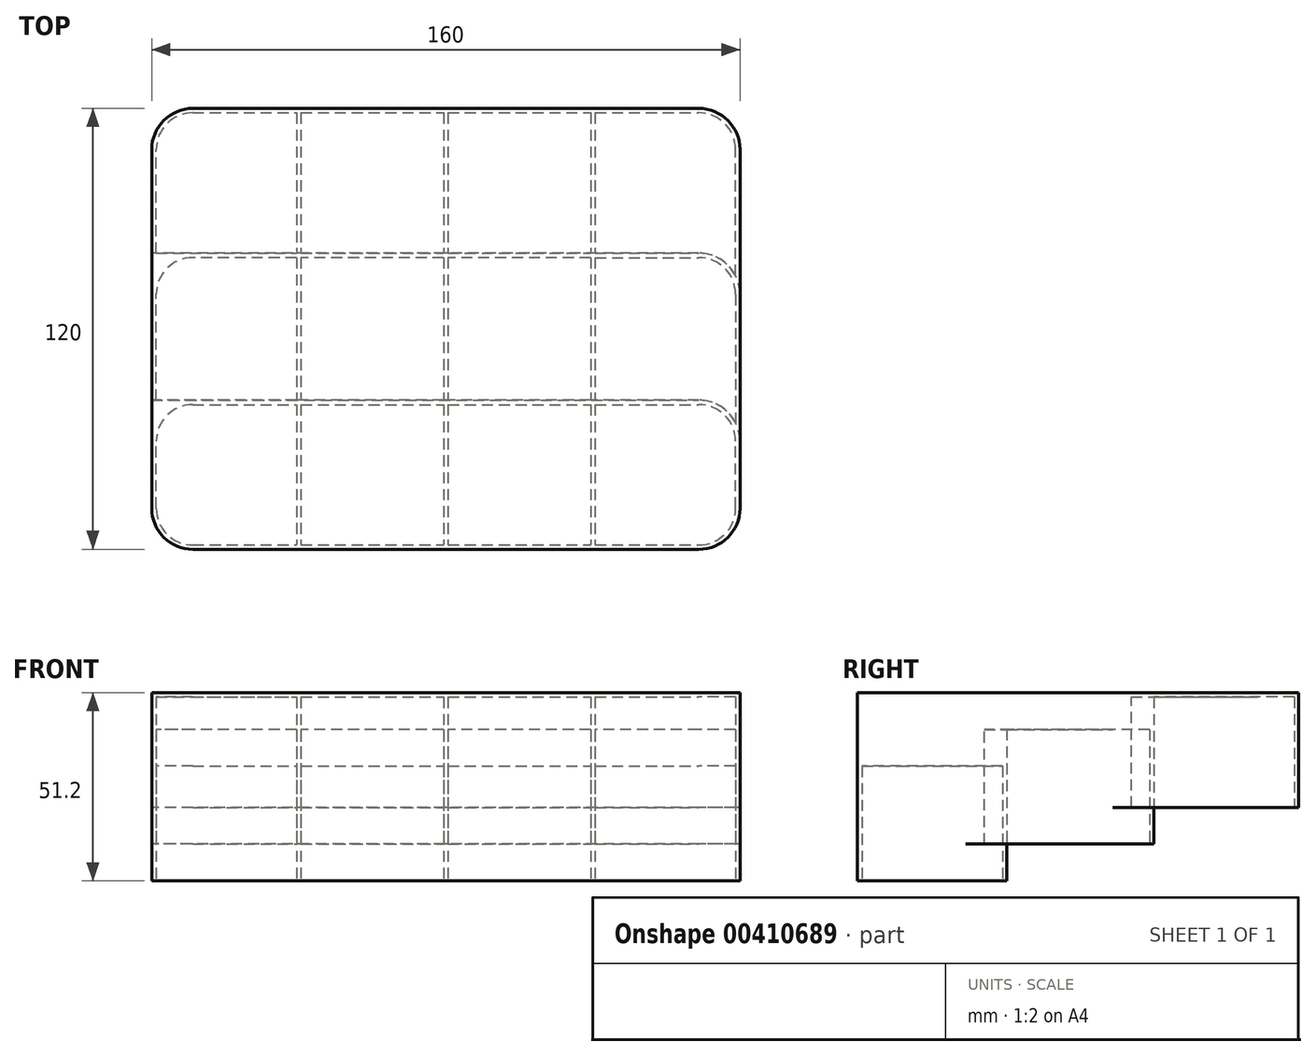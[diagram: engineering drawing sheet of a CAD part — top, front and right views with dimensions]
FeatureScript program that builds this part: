
annotation { "Feature Type Name" : "Feature", "Feature Type Description" : "" }
export const myFeature = defineFeature(function(context is Context, id is Id, definition is map)
    precondition{}
    {
        {
            var Q0;
            Q0=qCreatedBy(makeId("Top.planeOp"),FACE);
            var sketch = newSketch(context, id + "F0", { "sketchPlane" : qUnion([Q0])});
            skLineSegment(sketch, "E0.bottom", {"start": v(-160, -120) * mm, "end": v(0, -120) * mm});
            skLineSegment(sketch, "E0.top", {"start": v(-160, 0) * mm, "end": v(0, 0) * mm});
            skLineSegment(sketch, "E0.left", {"start": v(-160, -120) * mm, "end": v(-160, 0) * mm});
            skLineSegment(sketch, "E0.right", {"start": v(0, -120) * mm, "end": v(0, 0) * mm});
            skLineSegment(sketch, "E1.0", {"start": v(-158.8, -1.2) * mm, "end": v(-120.6, -1.2) * mm});
            skLineSegment(sketch, "E2.0", {"start": v(-158.8, -118.8) * mm, "end": v(-158.8, -80.6) * mm});
            skLineSegment(sketch, "E3.0", {"start": v(-158.8, -118.8) * mm, "end": v(-120.6, -118.8) * mm});
            skLineSegment(sketch, "E4.0", {"start": v(-1.2, -118.8) * mm, "end": v(-1.2, -80.6) * mm});
            skLineSegment(sketch, "E5.0", {"start": v(-158.8, -40.6) * mm, "end": v(-120.6, -40.6) * mm});
            skLineSegment(sketch, "E6.0", {"start": v(-158.8, -80.6) * mm, "end": v(-120.6, -80.6) * mm});
            skLineSegment(sketch, "E7.0", {"start": v(-158.8, -79.4) * mm, "end": v(-120.6, -79.4) * mm});
            skLineSegment(sketch, "E8.0", {"start": v(-158.8, -39.4) * mm, "end": v(-120.6, -39.4) * mm});
            skLineSegment(sketch, "E9.0", {"start": v(-120.6, -1.2) * mm, "end": v(-120.6, -39.4) * mm});
            skLineSegment(sketch, "E10.0", {"start": v(-119.4, -1.2) * mm, "end": v(-119.4, -39.4) * mm});
            skLineSegment(sketch, "E11.0", {"start": v(-80.6, -1.2) * mm, "end": v(-80.6, -39.4) * mm});
            skLineSegment(sketch, "E12.0", {"start": v(-79.4, -1.2) * mm, "end": v(-79.4, -39.4) * mm});
            skLineSegment(sketch, "E13.0", {"start": v(-40.6, -1.2) * mm, "end": v(-40.6, -39.4) * mm});
            skLineSegment(sketch, "E14.0", {"start": v(-39.4, -1.2) * mm, "end": v(-39.4, -39.4) * mm});
            skPoint(sketch, "E15.orphan", {"position": v(-160, -40) * mm});
            skLineSegment(sketch, "E16.trimOffspring", {"start": v(-158.8, -79.4) * mm, "end": v(-158.8, -40.6) * mm});
            skPoint(sketch, "E17.orphan", {"position": v(-160, -80) * mm});
            skPoint(sketch, "E18.orphan", {"position": v(-120, -120) * mm});
            skPoint(sketch, "E19.orphan", {"position": v(-80, -120) * mm});
            skPoint(sketch, "E20.orphan", {"position": v(0, -40) * mm});
            skLineSegment(sketch, "E21.trimOffspring", {"start": v(-119.4, -39.4) * mm, "end": v(-80.6, -39.4) * mm});
            skLineSegment(sketch, "E22.trimOffspring", {"start": v(-119.4, -40.6) * mm, "end": v(-80.6, -40.6) * mm});
            skLineSegment(sketch, "E23.trimOffspring", {"start": v(-120.6, -40.6) * mm, "end": v(-120.6, -79.4) * mm});
            skLineSegment(sketch, "E24.trimOffspring", {"start": v(-119.4, -40.6) * mm, "end": v(-119.4, -79.4) * mm});
            skLineSegment(sketch, "E25.trimOffspring", {"start": v(-119.4, -79.4) * mm, "end": v(-80.6, -79.4) * mm});
            skLineSegment(sketch, "E26.trimOffspring", {"start": v(-120.6, -80.6) * mm, "end": v(-120.6, -118.8) * mm});
            skLineSegment(sketch, "E27.trimOffspring", {"start": v(-119.4, -80.6) * mm, "end": v(-119.4, -118.8) * mm});
            skLineSegment(sketch, "E28.trimOffspring", {"start": v(-119.4, -80.6) * mm, "end": v(-80.6, -80.6) * mm});
            skLineSegment(sketch, "E29.trimOffspring", {"start": v(-80.6, -40.6) * mm, "end": v(-80.6, -79.4) * mm});
            skLineSegment(sketch, "E30.trimOffspring", {"start": v(-79.4, -39.4) * mm, "end": v(-40.6, -39.4) * mm});
            skLineSegment(sketch, "E31.trimOffspring", {"start": v(-79.4, -40.6) * mm, "end": v(-79.4, -79.4) * mm});
            skLineSegment(sketch, "E32.trimOffspring", {"start": v(-79.4, -40.6) * mm, "end": v(-40.6, -40.6) * mm});
            skLineSegment(sketch, "E33.trimOffspring", {"start": v(-40.6, -40.6) * mm, "end": v(-40.6, -79.4) * mm});
            skLineSegment(sketch, "E34.trimOffspring", {"start": v(-39.4, -39.4) * mm, "end": v(-1.2, -39.4) * mm});
            skLineSegment(sketch, "E35.trimOffspring", {"start": v(-39.4, -40.6) * mm, "end": v(-1.2, -40.6) * mm});
            skLineSegment(sketch, "E36.trimOffspring", {"start": v(-39.4, -40.6) * mm, "end": v(-39.4, -79.4) * mm});
            skLineSegment(sketch, "E37.trimOffspring", {"start": v(-39.4, -79.4) * mm, "end": v(-1.2, -79.4) * mm});
            skLineSegment(sketch, "E38.trimOffspring", {"start": v(-39.4, -80.6) * mm, "end": v(-1.2, -80.6) * mm});
            skLineSegment(sketch, "E39.trimOffspring", {"start": v(-39.4, -80.6) * mm, "end": v(-39.4, -118.8) * mm});
            skLineSegment(sketch, "E40.trimOffspring", {"start": v(-40.6, -80.6) * mm, "end": v(-40.6, -118.8) * mm});
            skLineSegment(sketch, "E41.trimOffspring", {"start": v(-79.4, -79.4) * mm, "end": v(-40.6, -79.4) * mm});
            skLineSegment(sketch, "E42.trimOffspring", {"start": v(-79.4, -80.6) * mm, "end": v(-40.6, -80.6) * mm});
            skLineSegment(sketch, "E43.trimOffspring", {"start": v(-80.6, -80.6) * mm, "end": v(-80.6, -118.8) * mm});
            skLineSegment(sketch, "E44.trimOffspring", {"start": v(-79.4, -80.6) * mm, "end": v(-79.4, -118.8) * mm});
            skLineSegment(sketch, "E45.trimOffspring", {"start": v(-1.2, -79.4) * mm, "end": v(-1.2, -40.6) * mm});
            skLineSegment(sketch, "E46.trimOffspring", {"start": v(-1.2, -39.4) * mm, "end": v(-1.2, -1.2) * mm});
            skLineSegment(sketch, "E47.trimOffspring", {"start": v(-39.4, -1.2) * mm, "end": v(-1.2, -1.2) * mm});
            skLineSegment(sketch, "E48.trimOffspring", {"start": v(-79.4, -1.2) * mm, "end": v(-40.6, -1.2) * mm});
            skLineSegment(sketch, "E49.trimOffspring", {"start": v(-119.4, -1.2) * mm, "end": v(-80.6, -1.2) * mm});
            skLineSegment(sketch, "E50.trimOffspring", {"start": v(-158.8, -39.4) * mm, "end": v(-158.8, -1.2) * mm});
            skLineSegment(sketch, "E51.trimOffspring", {"start": v(-119.4, -118.8) * mm, "end": v(-80.6, -118.8) * mm});
            skLineSegment(sketch, "E52.trimOffspring", {"start": v(-79.4, -118.8) * mm, "end": v(-40.6, -118.8) * mm});
            skLineSegment(sketch, "E53.trimOffspring", {"start": v(-39.4, -118.8) * mm, "end": v(-1.2, -118.8) * mm});
            skSolve(sketch);
        }
        {
            var Q0;
            Q0=makeQuery(id+"F0.imprint","IMPRINT",FACE,{"disambiguationData":[TD([[makeQuery(id+"F0.imprint","IMPRINT",EDGE,{"derivedFrom":sQuery(id+"F0.wireOp",EDGE,"E0.bottom")}),1.0]])]});
            extrude(context, id + "F1", {"entities" : qUnion([Q0]), "depth" : 50 * mm});
        }
        {
            var Q0;
            Q0=makeQuery(id+"F1.opExtrude","CAP_FACE",FACE,{"disambiguationData":[OSD([sQuery(id+"F0.wireOp",EDGE,"E0.bottom"),sQuery(id+"F0.wireOp",EDGE,"E0.top"),sQuery(id+"F0.wireOp",EDGE,"E0.left"),sQuery(id+"F0.wireOp",EDGE,"E0.right"),sQuery(id+"F0.wireOp",EDGE,"E1.0"),sQuery(id+"F0.wireOp",EDGE,"E2.0"),sQuery(id+"F0.wireOp",EDGE,"E3.0"),sQuery(id+"F0.wireOp",EDGE,"E4.0"),sQuery(id+"F0.wireOp",EDGE,"E5.0"),sQuery(id+"F0.wireOp",EDGE,"E6.0"),sQuery(id+"F0.wireOp",EDGE,"E7.0"),sQuery(id+"F0.wireOp",EDGE,"E8.0"),sQuery(id+"F0.wireOp",EDGE,"E9.0"),sQuery(id+"F0.wireOp",EDGE,"E10.0"),sQuery(id+"F0.wireOp",EDGE,"E11.0"),sQuery(id+"F0.wireOp",EDGE,"E12.0"),sQuery(id+"F0.wireOp",EDGE,"E13.0"),sQuery(id+"F0.wireOp",EDGE,"E14.0"),sQuery(id+"F0.wireOp",EDGE,"E16.trimOffspring"),sQuery(id+"F0.wireOp",EDGE,"E21.trimOffspring"),sQuery(id+"F0.wireOp",EDGE,"E22.trimOffspring"),sQuery(id+"F0.wireOp",EDGE,"E23.trimOffspring"),sQuery(id+"F0.wireOp",EDGE,"E24.trimOffspring"),sQuery(id+"F0.wireOp",EDGE,"E25.trimOffspring"),sQuery(id+"F0.wireOp",EDGE,"E26.trimOffspring"),sQuery(id+"F0.wireOp",EDGE,"E27.trimOffspring"),sQuery(id+"F0.wireOp",EDGE,"E28.trimOffspring"),sQuery(id+"F0.wireOp",EDGE,"E29.trimOffspring"),sQuery(id+"F0.wireOp",EDGE,"E30.trimOffspring"),sQuery(id+"F0.wireOp",EDGE,"E31.trimOffspring"),sQuery(id+"F0.wireOp",EDGE,"E32.trimOffspring"),sQuery(id+"F0.wireOp",EDGE,"E33.trimOffspring"),sQuery(id+"F0.wireOp",EDGE,"E34.trimOffspring"),sQuery(id+"F0.wireOp",EDGE,"E35.trimOffspring"),sQuery(id+"F0.wireOp",EDGE,"E36.trimOffspring"),sQuery(id+"F0.wireOp",EDGE,"E37.trimOffspring"),sQuery(id+"F0.wireOp",EDGE,"E38.trimOffspring"),sQuery(id+"F0.wireOp",EDGE,"E39.trimOffspring"),sQuery(id+"F0.wireOp",EDGE,"E40.trimOffspring"),sQuery(id+"F0.wireOp",EDGE,"E41.trimOffspring"),sQuery(id+"F0.wireOp",EDGE,"E42.trimOffspring"),sQuery(id+"F0.wireOp",EDGE,"E43.trimOffspring"),sQuery(id+"F0.wireOp",EDGE,"E44.trimOffspring"),sQuery(id+"F0.wireOp",EDGE,"E45.trimOffspring"),sQuery(id+"F0.wireOp",EDGE,"E46.trimOffspring"),sQuery(id+"F0.wireOp",EDGE,"E47.trimOffspring"),sQuery(id+"F0.wireOp",EDGE,"E48.trimOffspring"),sQuery(id+"F0.wireOp",EDGE,"E49.trimOffspring"),sQuery(id+"F0.wireOp",EDGE,"E50.trimOffspring"),sQuery(id+"F0.wireOp",EDGE,"E51.trimOffspring"),sQuery(id+"F0.wireOp",EDGE,"E52.trimOffspring"),sQuery(id+"F0.wireOp",EDGE,"E53.trimOffspring")])],"isStart":false});
            var sketch = newSketch(context, id + "F2", { "sketchPlane" : qUnion([Q0])});
            skLineSegment(sketch, "E54.bottom", {"start": v(-160, 0) * mm, "end": v(0, 0) * mm});
            skLineSegment(sketch, "E54.top", {"start": v(-160, -120) * mm, "end": v(0, -120) * mm});
            skLineSegment(sketch, "E54.left", {"start": v(-160, 0) * mm, "end": v(-160, -120) * mm});
            skLineSegment(sketch, "E54.right", {"start": v(0, 0) * mm, "end": v(0, -120) * mm});
            skSolve(sketch);
        }
        {
            var Q0;
            Q0 = qSketchRegion(id + "F2", true);
            extrude(context, id + "F3", {"entities" : qUnion([Q0]), "operationType" : NewBodyOperationType.ADD, "depth" : 1.2 * mm});
        }
        {
            var Q0;
            Q0=makeQuery(id+"F3.boolean.opBoolean","MERGE",FACE,{"derivedFrom":[makeQuery(id+"F1.opExtrude","SWEPT_FACE",FACE,{"disambiguationData":[OSD([sQuery(id+"F0.wireOp",EDGE,"E0.left")])]}),makeQuery(id+"F3.opExtrude","SWEPT_FACE",FACE,{"disambiguationData":[OSD([sQuery(id+"F2.wireOp",EDGE,"E54.left")])]})]});
            var sketch = newSketch(context, id + "F4", { "sketchPlane" : qUnion([Q0])});
            skLineSegment(sketch, "E55.0.0", {"start": v(79.4, 0) * mm, "end": v(40.6, 0) * mm, "construction": true});
            skLineSegment(sketch, "E55.0.1", {"start": v(40.6, 10) * mm, "end": v(40.6, 50) * mm, "construction": true});
            skLineSegment(sketch, "E55.0.2", {"start": v(40.6, 50) * mm, "end": v(79.4, 50) * mm, "construction": true});
            skLineSegment(sketch, "E55.0.3", {"start": v(79.4, 50) * mm, "end": v(79.4, 0) * mm, "construction": true});
            skLineSegment(sketch, "E56.0.0", {"start": v(39.4, 0) * mm, "end": v(1.2, 0) * mm, "construction": true});
            skLineSegment(sketch, "E56.0.1", {"start": v(1.2, 20) * mm, "end": v(1.2, 50) * mm, "construction": true});
            skLineSegment(sketch, "E56.0.2", {"start": v(1.2, 50) * mm, "end": v(39.4, 50) * mm, "construction": true});
            skLineSegment(sketch, "E56.0.3", {"start": v(39.4, 50) * mm, "end": v(39.4, 10) * mm, "construction": true});
            skLineSegment(sketch, "E57", {"start": v(79.4, 0) * mm, "end": v(79.4, 10) * mm, "construction": true});
            skLineSegment(sketch, "E58", {"start": v(79.4, 10) * mm, "end": v(39.4, 10) * mm, "construction": true});
            skLineSegment(sketch, "E59", {"start": v(39.4, 10) * mm, "end": v(39.4, 20) * mm, "construction": true});
            skLineSegment(sketch, "E60", {"start": v(39.4, 20) * mm, "end": v(0, 20) * mm, "construction": true});
            skLineSegment(sketch, "E61", {"start": v(79.4, 10) * mm, "end": v(39.4, 10) * mm});
            skLineSegment(sketch, "E62", {"start": v(39.4, 20) * mm, "end": v(39.4, 10) * mm});
            skLineSegment(sketch, "E63", {"start": v(39.4, 20) * mm, "end": v(0, 20) * mm});
            skLineSegment(sketch, "E64", {"start": v(0, 20) * mm, "end": v(0, 0) * mm});
            skLineSegment(sketch, "E65", {"start": v(0, 0) * mm, "end": v(79.4, 0) * mm});
            skLineSegment(sketch, "E66", {"start": v(79.4, 10) * mm, "end": v(79.4, 0) * mm});
            skSolve(sketch);
        }
        {
            var Q0;
            Q0=makeQuery(id+"F4.imprint","IMPRINT",FACE,{"disambiguationData":[TD([[makeQuery(id+"F4.imprint","IMPRINT",EDGE,{"derivedFrom":sQuery(id+"F4.wireOp",EDGE,"E61")}),1.0]])]});
            extrude(context, id + "F5", {"entities" : qUnion([Q0]), "operationType" : NewBodyOperationType.REMOVE, "endBound" : BoundingType.THROUGH_ALL, "oppositeDirection" : true, "depth" : 25 * mm});
        }
        {
            var Q0;
            Q0=makeQuery(id+"F3.boolean.opBoolean","MERGE",FACE,{"derivedFrom":[makeQuery(id+"F1.opExtrude","SWEPT_FACE",FACE,{"disambiguationData":[OSD([sQuery(id+"F0.wireOp",EDGE,"E0.left")])]}),makeQuery(id+"F3.opExtrude","SWEPT_FACE",FACE,{"disambiguationData":[OSD([sQuery(id+"F2.wireOp",EDGE,"E54.left")])]})]});
            var sketch = newSketch(context, id + "F6", { "sketchPlane" : qUnion([Q0])});
            skLineSegment(sketch, "E67.0.0", {"start": v(80.6, 0) * mm, "end": v(118.8, 0) * mm});
            skLineSegment(sketch, "E67.0.1", {"start": v(118.8, 31.2) * mm, "end": v(118.8, 50) * mm});
            skLineSegment(sketch, "E67.0.2", {"start": v(118.8, 50) * mm, "end": v(40.6, 50) * mm});
            skLineSegment(sketch, "E68.0.0", {"start": v(40.6, 50) * mm, "end": v(40.6, 10) * mm});
            skLineSegment(sketch, "E68.0.1", {"start": v(40.6, 10) * mm, "end": v(79.4, 10) * mm});
            skLineSegment(sketch, "E68.0.2", {"start": v(79.4, 31.2) * mm, "end": v(79.4, 41.2) * mm});
            skLineSegment(sketch, "E69", {"start": v(118.8, 31.2) * mm, "end": v(79.4, 31.2) * mm});
            skLineSegment(sketch, "E70", {"start": v(79.4, 41.2) * mm, "end": v(40.6, 41.2) * mm});
            skPoint(sketch, "E71.orphan", {"position": v(80.6, 50) * mm});
            skSolve(sketch);
        }
        {
            var Q0;
            Q0=makeQuery(id+"F6.imprint","IMPRINT",FACE,{"disambiguationData":[TD([[makeQuery(id+"F6.imprint","IMPRINT",EDGE,{"derivedFrom":sQuery(id+"F6.wireOp",EDGE,"E67.0.1")}),1.0]])]});
            var Q1;
            Q1=makeQuery(id+"F1.opExtrude","SWEPT_FACE",FACE,{"disambiguationData":[OSD([sQuery(id+"F0.wireOp",EDGE,"E45.trimOffspring")])]});
            extrude(context, id + "F7", {"entities" : qUnion([Q0]), "operationType" : NewBodyOperationType.ADD, "endBound" : BoundingType.UP_TO_SURFACE, "oppositeDirection" : true, "endBoundEntityFace" : qUnion([Q1]), "depth" : 25 * mm});
        }
        {
            var Q0;
            Q0=makeQuery(id+"F1.opExtrude","SWEPT_EDGE",EDGE,{"disambiguationData":[OSD([sQuery(id+"F0.wireOp",EDGE,"E4.0"),sQuery(id+"F0.wireOp",EDGE,"E53.trimOffspring")])]});
            var Q1;
            Q1=makeQuery(id+"F1.opExtrude","SWEPT_EDGE",EDGE,{"disambiguationData":[OSD([sQuery(id+"F0.wireOp",EDGE,"E46.trimOffspring"),sQuery(id+"F0.wireOp",EDGE,"E47.trimOffspring")])]});
            var Q2;
            Q2=makeQuery(id+"F1.opExtrude","SWEPT_EDGE",EDGE,{"disambiguationData":[OSD([sQuery(id+"F0.wireOp",EDGE,"E2.0"),sQuery(id+"F0.wireOp",EDGE,"E3.0")])]});
            var Q3;
            Q3=makeQuery(id+"F1.opExtrude","SWEPT_EDGE",EDGE,{"disambiguationData":[OSD([sQuery(id+"F0.wireOp",EDGE,"E1.0"),sQuery(id+"F0.wireOp",EDGE,"E50.trimOffspring")])]});
            fillet(context, id + "F8", {"entities" : qUnion([Q0, Q1, Q2, Q3]), "radius" : 10 * mm, "tangentPropagation" : true, "allowEdgeOverflow" : false});
        }
        {
            var Q0;
            Q0=makeQuery(id+"F3.boolean.opBoolean","MERGE",EDGE,{"derivedFrom":[makeQuery(id+"F1.opExtrude","SWEPT_EDGE",EDGE,{"disambiguationData":[OSD([sQuery(id+"F0.wireOp",EDGE,"E0.top"),sQuery(id+"F0.wireOp",EDGE,"E0.left")])]}),makeQuery(id+"F3.opExtrude","SWEPT_EDGE",EDGE,{"disambiguationData":[OSD([sQuery(id+"F2.wireOp",EDGE,"E54.bottom"),sQuery(id+"F2.wireOp",EDGE,"E54.left")])]})]});
            var Q1;
            Q1=makeQuery(id+"F3.boolean.opBoolean","MERGE",EDGE,{"derivedFrom":[makeQuery(id+"F1.opExtrude","SWEPT_EDGE",EDGE,{"disambiguationData":[OSD([sQuery(id+"F0.wireOp",EDGE,"E0.top"),sQuery(id+"F0.wireOp",EDGE,"E0.right")])]}),makeQuery(id+"F3.opExtrude","SWEPT_EDGE",EDGE,{"disambiguationData":[OSD([sQuery(id+"F2.wireOp",EDGE,"E54.bottom"),sQuery(id+"F2.wireOp",EDGE,"E54.right")])]})]});
            var Q2;
            Q2=makeQuery(id+"F3.boolean.opBoolean","MERGE",EDGE,{"derivedFrom":[makeQuery(id+"F1.opExtrude","SWEPT_EDGE",EDGE,{"disambiguationData":[OSD([sQuery(id+"F0.wireOp",EDGE,"E0.bottom"),sQuery(id+"F0.wireOp",EDGE,"E0.right")])]}),makeQuery(id+"F3.opExtrude","SWEPT_EDGE",EDGE,{"disambiguationData":[OSD([sQuery(id+"F2.wireOp",EDGE,"E54.top"),sQuery(id+"F2.wireOp",EDGE,"E54.right")])]})]});
            var Q3;
            Q3=makeQuery(id+"F3.boolean.opBoolean","MERGE",EDGE,{"derivedFrom":[makeQuery(id+"F1.opExtrude","SWEPT_EDGE",EDGE,{"disambiguationData":[OSD([sQuery(id+"F0.wireOp",EDGE,"E0.bottom"),sQuery(id+"F0.wireOp",EDGE,"E0.left")])]}),makeQuery(id+"F3.opExtrude","SWEPT_EDGE",EDGE,{"disambiguationData":[OSD([sQuery(id+"F2.wireOp",EDGE,"E54.top"),sQuery(id+"F2.wireOp",EDGE,"E54.left")])]})]});
            fillet(context, id + "F9", {"entities" : qUnion([Q0, Q1, Q2, Q3]), "radius" : 11.2 * mm, "tangentPropagation" : true, "allowEdgeOverflow" : false});
        }
        {
            var Q0;
            Q0=makeQuery(id+"F1.opExtrude","SWEPT_EDGE",EDGE,{"disambiguationData":[OSD([sQuery(id+"F0.wireOp",EDGE,"E2.0"),sQuery(id+"F0.wireOp",EDGE,"E6.0")])]});
            var Q1;
            Q1=makeQuery(id+"F1.opExtrude","SWEPT_EDGE",EDGE,{"disambiguationData":[OSD([sQuery(id+"F0.wireOp",EDGE,"E5.0"),sQuery(id+"F0.wireOp",EDGE,"E16.trimOffspring")])]});
            var Q2;
            Q2=makeQuery(id+"F1.opExtrude","SWEPT_EDGE",EDGE,{"disambiguationData":[OSD([sQuery(id+"F0.wireOp",EDGE,"E35.trimOffspring"),sQuery(id+"F0.wireOp",EDGE,"E45.trimOffspring")])]});
            var Q3;
            Q3=makeQuery(id+"F1.opExtrude","SWEPT_EDGE",EDGE,{"disambiguationData":[OSD([sQuery(id+"F0.wireOp",EDGE,"E4.0"),sQuery(id+"F0.wireOp",EDGE,"E38.trimOffspring")])]});
            fillet(context, id + "F10", {"entities" : qUnion([Q0, Q1, Q2, Q3]), "radius" : 10 * mm, "tangentPropagation" : true, "allowEdgeOverflow" : false});
        }
        {
            var Q0;
            Q0=makeQuery(id+"F5.boolean.opBoolean","COPY",EDGE,{"derivedFrom":makeQuery(id+"F5.opExtrude","CAP_EDGE",EDGE,{"disambiguationData":[OSD([sQuery(id+"F4.wireOp",EDGE,"E66")])],"isStart":true})});
            var Q1;
            Q1=makeQuery(id+"F5.boolean.opBoolean","COPY",EDGE,{"derivedFrom":makeQuery(id+"F5.opExtrude","CAP_EDGE",EDGE,{"disambiguationData":[OSD([sQuery(id+"F4.wireOp",EDGE,"E62")])],"isStart":true})});
            var Q2;
            Q2=makeQuery(id+"F5.boolean.opBoolean","INTERSECT",EDGE,{"derivedFrom":[makeQuery(id+"F3.boolean.opBoolean","MERGE",FACE,{"derivedFrom":[makeQuery(id+"F1.opExtrude","SWEPT_FACE",FACE,{"disambiguationData":[OSD([sQuery(id+"F0.wireOp",EDGE,"E0.right")])]}),makeQuery(id+"F3.opExtrude","SWEPT_FACE",FACE,{"disambiguationData":[OSD([sQuery(id+"F2.wireOp",EDGE,"E54.right")])]})]}),makeQuery(id+"F5.opExtrude","SWEPT_FACE",FACE,{"disambiguationData":[OSD([sQuery(id+"F4.wireOp",EDGE,"E66")])]})]});
            var Q3;
            Q3=makeQuery(id+"F5.boolean.opBoolean","INTERSECT",EDGE,{"derivedFrom":[makeQuery(id+"F3.boolean.opBoolean","MERGE",FACE,{"derivedFrom":[makeQuery(id+"F1.opExtrude","SWEPT_FACE",FACE,{"disambiguationData":[OSD([sQuery(id+"F0.wireOp",EDGE,"E0.right")])]}),makeQuery(id+"F3.opExtrude","SWEPT_FACE",FACE,{"disambiguationData":[OSD([sQuery(id+"F2.wireOp",EDGE,"E54.right")])]})]}),makeQuery(id+"F5.opExtrude","SWEPT_FACE",FACE,{"disambiguationData":[OSD([sQuery(id+"F4.wireOp",EDGE,"E62")])]})]});
            fillet(context, id + "F11", {"entities" : qUnion([Q0, Q1, Q2, Q3]), "radius" : 11.2 * mm, "tangentPropagation" : true, "allowEdgeOverflow" : false});
        }
    });
